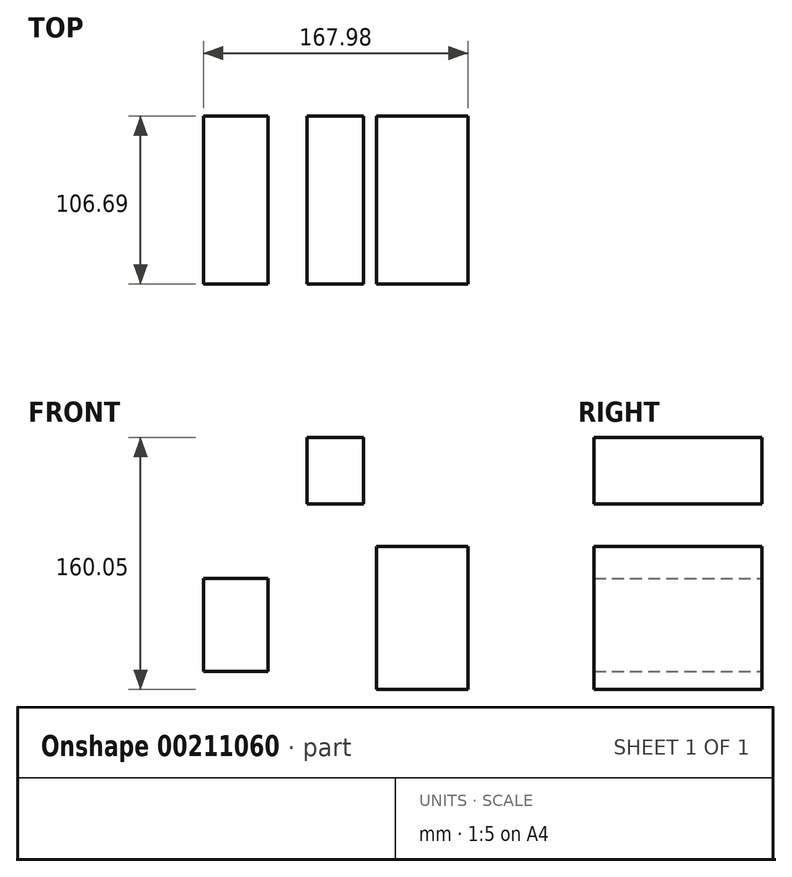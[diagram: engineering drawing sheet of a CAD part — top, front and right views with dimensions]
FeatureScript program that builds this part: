
annotation { "Feature Type Name" : "Feature", "Feature Type Description" : "" }
export const myFeature = defineFeature(function(context is Context, id is Id, definition is map)
    precondition{}
    {
        {
            var Q0;
            Q0=qCreatedBy(makeId("Front.planeOp"),FACE);
            var sketch = newSketch(context, id + "F0", { "sketchPlane" : qUnion([Q0])});
            skLineSegment(sketch, "E0.bottom", {"start": v(-14.05, 130.63) * mm, "end": v(21.95, 130.63) * mm});
            skLineSegment(sketch, "E0.top", {"start": v(-14.05, 88.31) * mm, "end": v(21.95, 88.31) * mm});
            skLineSegment(sketch, "E0.left", {"start": v(-14.05, 130.63) * mm, "end": v(-14.05, 88.31) * mm});
            skLineSegment(sketch, "E0.right", {"start": v(21.95, 130.63) * mm, "end": v(21.95, 88.31) * mm});
            skLineSegment(sketch, "E1.bottom", {"start": v(-79.77, 41.17) * mm, "end": v(-38.89, 41.17) * mm});
            skLineSegment(sketch, "E1.top", {"start": v(-79.77, -18.06) * mm, "end": v(-38.89, -18.06) * mm});
            skLineSegment(sketch, "E1.left", {"start": v(-79.77, 41.17) * mm, "end": v(-79.77, -18.06) * mm});
            skLineSegment(sketch, "E1.right", {"start": v(-38.89, 41.17) * mm, "end": v(-38.89, -18.06) * mm});
            skLineSegment(sketch, "E2.bottom", {"start": v(29.98, 61.57) * mm, "end": v(88.21, 61.57) * mm});
            skLineSegment(sketch, "E2.top", {"start": v(29.98, -29.42) * mm, "end": v(88.21, -29.42) * mm});
            skLineSegment(sketch, "E2.left", {"start": v(29.98, 61.57) * mm, "end": v(29.98, -29.42) * mm});
            skLineSegment(sketch, "E2.right", {"start": v(88.21, 61.57) * mm, "end": v(88.21, -29.42) * mm});
            skSolve(sketch);
        }
        {
            var Q0;
            Q0 = qSketchRegion(id + "F0", true);
            extrude(context, id + "F1", {"entities" : qUnion([Q0]), "depth" : 106.7 * mm});
        }
    });
